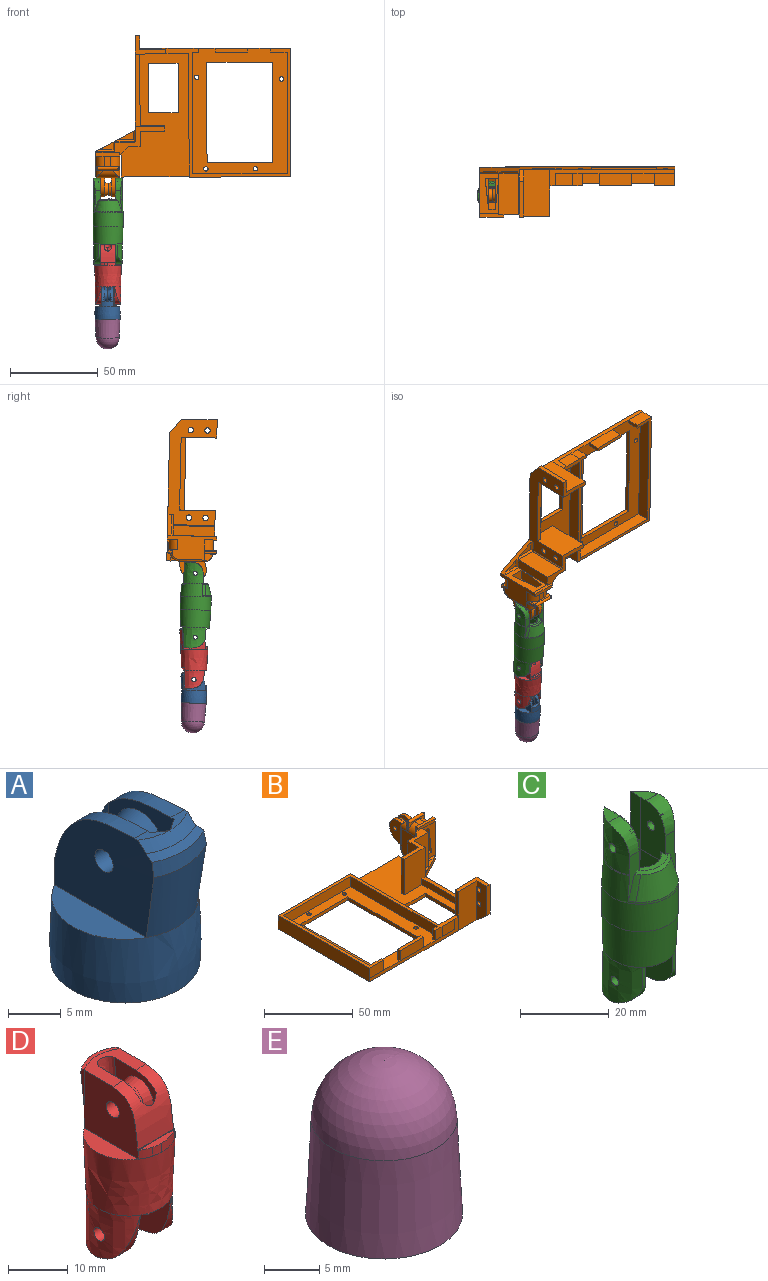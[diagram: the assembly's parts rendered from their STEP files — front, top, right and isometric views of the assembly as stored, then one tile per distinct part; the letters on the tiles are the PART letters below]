
ASSEMBLY  parts=5 mates=4
PART A: 32 faces, bbox 15x16.1x19 mm
  f0: bspline ~6.52x6.52mm, area 30.3mm2, adj f2,f3
  f1: plane 6.53x6.53mm, normal (-1,0,0), area 28.8mm2, adj f2,f31
  f2: bspline ~6.52x6.52mm, area 30.3mm2, adj f0,f1
  f3: plane 13x9.4mm, normal (-1,0,0), area 76.2mm2, adj f0,f4,f8,f11,f17,f19,f26,f27
  f4: plane 6.65x3.21mm, normal (0,0,1), area 9.7mm2, adj f3,f8,f9,f10,f12,f19,f20,f26
  f5: plane 3.24x1.42mm, normal (0,0,1), area 2.2mm2, adj f6,f9,f18,f20,f21
  f6: plane 13.3x11.06mm, normal (-1,0,0), area 116.5mm2, adj f5,f12,f15,f20,f21,f23,f24,f25
  f7: plane 12.34x11.06mm, normal (1,0,0), area 111mm2, adj f11,f12,f16,f19,f21,f22,f31
  f8: plane 5.75x3.05mm, normal (-0.96,0.27,0), area 7.6mm2, adj f3,f4,f19
  f9: plane 13x9.4mm, normal (1,0,0), area 104.9mm2, adj f4,f5,f10,f18,f20,f26,f27,f30
  f10: plane 5.75x3.05mm, normal (0.96,0.27,0), area 7.6mm2, adj f4,f9,f20
  f11: plane 3.24x1.42mm, normal (0,0,1), area 2.2mm2, adj f3,f7,f17,f19,f21
  f12: bspline ~8.52x3.23mm, area 22.2mm2, adj f4,f6,f7,f14
  f13: plane 14.18x14.18mm, normal (0,0,-1), area 149.3mm2, adj f14,f28,f29
  f14: bspline ~14.35x14.35mm, area 327.8mm2, adj f12,f13,f15,f16,f23
  f15: plane 12.33x3.71mm, normal (0,0,1), area 31.9mm2, adj f6,f14
  f16: plane 12.36x3.74mm, normal (0,0,1), area 31.9mm2, adj f7,f14
  f17: plane 12.71x1.56mm, normal (-0.56,0.83,0), area 24mm2, adj f3,f11,f18,f21,f27
  f18: plane 12.71x1.56mm, normal (0.56,0.83,0), area 24mm2, adj f5,f9,f17,f21,f27
  f19: extruded ~10.69x7.52mm, area 23.8mm2, adj f3,f4,f7,f8,f11
  f20: extruded ~10.69x7.52mm, area 23.8mm2, adj f4,f5,f6,f9,f10
  f21: bspline ~8.22x2.15mm, area 9.9mm2, adj f5,f6,f7,f11,f17,f18,f25
  f22: plane 9.73x0.86mm, normal (0.55,0.84,0), area 5.5mm2, adj f7,f23,f24,f25
  f23: bspline ~7.5x7.44mm, area 55.3mm2, adj f6,f14,f22,f24
  f24: bspline ~7.5x1.72mm, area 12.7mm2, adj f6,f22,f23,f25
  f25: bspline ~7.28x1.87mm, area 6.8mm2, adj f6,f21,f22,f24
  f26: cylinder r=2.84mm len=5.19mm, axis (0,0,1), area 17.1mm2, adj f3,f4,f9,f27
  f27: plane 10.93x3.12mm, normal (0,0,1), area 23.5mm2, adj f3,f9,f17,f18,f26,f28,f29
  f28: cylinder r=1.16mm len=5.33mm, axis (0,0,-1), area 39mm2, adj f13,f27
  f29: cylinder r=1.16mm len=5.33mm, axis (0,0,-1), area 38.9mm2, adj f13,f27
  f30: cylinder r=1.22mm len=2.43mm, axis (-1,0,0), area 13.5mm2, adj f6,f9
  f31: cylinder r=1.22mm len=4.8mm, axis (-1,0,0), area 36.7mm2, adj f1,f7
PART B: 149 faces, bbox 111.3x92x28.5 mm
  f0: plane 60.18x26.89mm, normal (1,0,0), area 702.9mm2, adj f9,f23,f24,f32,f60,f63,f68,f70
  f1: plane 13.52x2.01mm, normal (0,-1,0), area 25.2mm2, adj f4,f21,f31,f63,f78,f94
  f2: plane 9.17x4.88mm, normal (0,0,1), area 22.4mm2, adj f32,f147,f148
  f3: plane 0.5x0.13mm, normal (0,-1,0), area 0mm2, adj f104,f117,f141
  f4: plane 27.22x13.53mm, normal (-1,0,0), area 230.8mm2, adj f1,f12,f63,f93,f94,f97,f99,f104
  f5: plane 14.04x11.79mm, normal (0,1,0), area 54mm2, adj f7,f16,f17,f107,f108,f110,f121,f124
  f6: plane 8.39x3.75mm, normal (0,-0.18,0.98), area 31.8mm2, adj f19,f20,f79,f91,f92,f108
  f7: extruded ~10.9x7.85mm, area 33.1mm2, adj f5,f10,f17,f85,f92
  f8: plane 83.12x9.32mm, normal (0,1,0), area 598.9mm2, adj f9,f12,f30,f42,f45,f106
  f9: plane 111x73.01mm, normal (0,0,-1), area 4099.4mm2, adj f0,f8,f26,f27,f28,f29,f30,f31
  f10: plane 2.53x2.22mm, normal (0,1,0), area 5.6mm2, adj f7,f17,f85,f88
  f11: plane 2.53x2.13mm, normal (0,1,0), area 5.4mm2, adj f15,f16,f90,f107
  f12: plane 70.48x39.53mm, normal (0,0,1), area 1630.3mm2, adj f4,f8,f24,f26,f27,f28,f41,f45
  f13: plane 6x3.53mm, normal (0,0,1), area 21.1mm2, adj f93,f96,f97,f98
  f14: plane 8.29x0mm, normal (0,0,1), area 0mm2, adj f15,f91,f107
  f15: plane 13.03x11.25mm, normal (-1,0,0), area 75.3mm2, adj f11,f14,f18,f19,f87,f90,f107,f110
  f16: plane 16.08x11.25mm, normal (1,0,0), area 134.2mm2, adj f5,f11,f89,f90,f107,f110
  f17: plane 16.08x11.25mm, normal (-1,0,0), area 134.2mm2, adj f5,f7,f10,f88,f89,f110
  f18: plane 3.72x0.75mm, normal (0,1,0), area 2.8mm2, adj f15,f84,f85,f110
  f19: plane 17.65x8.49mm, normal (-1,0,0), area 126mm2, adj f6,f15,f79,f84,f91
  f20: plane 17.65x8.49mm, normal (1,0,0), area 126mm2, adj f6,f79,f84,f85,f92
  f21: plane 22.91x10.84mm, normal (0,-1,0), area 145.8mm2, adj f1,f31,f78,f80,f81,f82,f83,f145
  f22: plane 7.94x4.22mm, normal (0,0,1), area 16.8mm2, adj f32,f145,f146
  f23: plane 20.29x2.59mm, normal (0,-1,0), area 52.5mm2, adj f0,f60,f62,f76
  f24: plane 30.4x24.56mm, normal (0,1,0), area 507.8mm2, adj f0,f12,f42,f45,f59,f60,f70,f71
  f25: plane 71x54mm, normal (0,0,1), area 1615.6mm2, adj f29,f33,f34,f35,f36,f37,f38,f39
  f26: plane 17.02x2.33mm, normal (0,-1,0), area 39.6mm2, adj f9,f12,f27,f41
  f27: plane 28.12x2.33mm, normal (1,0,0), area 65.5mm2, adj f9,f12,f26,f28
  f28: plane 17.02x2.33mm, normal (0,1,0), area 39.6mm2, adj f9,f12,f27,f41
  f29: plane 70.93x9.33mm, normal (0,-1,0), area 186.1mm2, adj f9,f25,f30,f42,f43,f44,f46,f55
  f30: plane 73x9.32mm, normal (-1,0,0), area 680.7mm2, adj f8,f9,f29,f42,f46
  f31: plane 28.22x13.51mm, normal (1,0,0), area 250.7mm2, adj f1,f9,f21,f32,f93,f94,f98,f99
  f32: plane 22.64x12.04mm, normal (0.47,-0.88,0), area 62.7mm2, adj f0,f2,f9,f22,f31,f145,f146,f147
  f33: plane 56.99x2.33mm, normal (1,0,0), area 132.7mm2, adj f9,f25,f34,f40
  f34: plane 37.47x2.33mm, normal (0,1,0), area 87.2mm2, adj f9,f25,f33,f35
  f35: plane 56.99x2.33mm, normal (-1,0,0), area 132.7mm2, adj f9,f25,f34,f40
  f36: cylinder r=1.25mm len=2.5mm, axis (0,0,-1), area 18.3mm2, adj f9,f25
  f37: cylinder r=1.25mm len=2.5mm, axis (0,0,-1), area 18.3mm2, adj f9,f25
  f38: cylinder r=1.25mm len=2.5mm, axis (0,0,-1), area 18.3mm2, adj f9,f25
  f39: cylinder r=1.25mm len=2.5mm, axis (0,0,-1), area 18.3mm2, adj f9,f25
  f40: plane 37.47x2.33mm, normal (0,-1,0), area 87.2mm2, adj f9,f25,f33,f35
  f41: plane 28.12x2.33mm, normal (-1,0,0), area 65.5mm2, adj f9,f12,f26,f28
  f42: plane 73.01x70.92mm, normal (0,0,1), area 455mm2, adj f8,f24,f29,f30,f43,f44,f45,f46
  f43: plane 7x5.46mm, normal (0,-1,0), area 38.1mm2, adj f29,f42,f44,f53
  f44: plane 9.98x7mm, normal (0,-1,0), area 69.8mm2, adj f29,f42,f43
  f45: plane 70.48x7mm, normal (1,0,0), area 493.1mm2, adj f8,f12,f24,f42
  f46: plane 11.5x7mm, normal (0,-1,0), area 80.5mm2, adj f29,f30,f42,f47
  f47: plane 7x2mm, normal (1,0,0), area 14mm2, adj f25,f42,f46,f48
  f48: plane 9.5x7mm, normal (0,1,0), area 66.4mm2, adj f25,f42,f47,f49
  f49: plane 68.99x7mm, normal (1,0,0), area 482.7mm2, adj f25,f42,f48,f50
  f50: plane 54x7mm, normal (0,-1,0), area 377.8mm2, adj f25,f42,f49,f51
  f51: plane 68.99x7mm, normal (-1,0,0), area 482.7mm2, adj f25,f42,f50,f52
  f52: plane 7x3.5mm, normal (0,1,0), area 24.5mm2, adj f25,f42,f51,f53
  f53: plane 7x2.01mm, normal (-1,0,0), area 14mm2, adj f25,f42,f43,f52
  f54: plane 18.5x2mm, normal (0,0,1), area 37.1mm2, adj f55,f56,f57,f58
  f55: plane 18.5x7mm, normal (0,-1,0), area 129.4mm2, adj f29,f54,f56,f57
  f56: plane 7x2.01mm, normal (1,0,0), area 14mm2, adj f25,f54,f55,f58
  f57: plane 7x2.01mm, normal (-1,0,0), area 14mm2, adj f25,f54,f55,f58
  f58: plane 18.5x7mm, normal (0,1,0), area 129.4mm2, adj f25,f54,f56,f57
  f59: plane 17.57x2.52mm, normal (-1,0,0), area 44.3mm2, adj f24,f42,f60,f61
  f60: plane 17.43x10.36mm, normal (0,0,1), area 64.2mm2, adj f0,f23,f24,f59,f61,f62
  f61: plane 26.89x14.85mm, normal (0,-1,0), area 399.2mm2, adj f9,f29,f59,f60,f62,f69
  f62: plane 26.89x7.84mm, normal (-1,0,0), area 169.9mm2, adj f23,f60,f61,f74,f75,f76
  f63: plane 28.55x16.27mm, normal (0,0,1), area 113.7mm2, adj f0,f1,f4,f64,f65,f66,f67,f68
  f64: plane 24.56x6.7mm, normal (0,1,0), area 164.6mm2, adj f12,f63,f65,f143
  f65: plane 24.56x8.75mm, normal (-1,0,0), area 200mm2, adj f12,f63,f64,f66,f72,f73
  f66: plane 24.56x14.14mm, normal (0,1,0), area 347.2mm2, adj f12,f63,f65,f67
  f67: plane 24.56x2.5mm, normal (-1,0,0), area 61.5mm2, adj f12,f63,f66,f68
  f68: plane 24.56x16.72mm, normal (0,-1,0), area 399.7mm2, adj f0,f12,f63,f67,f70,f71
  f69: plane 2.33x0mm, normal (-1,0,0), area 0mm2, adj f9,f29,f61
  f70: plane 41.42x2.59mm, normal (0,0,1), area 107.1mm2, adj f0,f24,f68,f71
  f71: plane 41.42x4.28mm, normal (-1,0,0), area 177.2mm2, adj f12,f24,f68,f70
  f72: cylinder r=1.54mm len=3.08mm, axis (1,0,0), area 25mm2, adj f0,f65
  f73: cylinder r=1.54mm len=3.08mm, axis (1,0,0), area 25mm2, adj f0,f65
  f74: cylinder r=1.54mm len=3.08mm, axis (1,0,0), area 25.1mm2, adj f0,f62
  f75: cylinder r=1.54mm len=3.08mm, axis (1,0,0), area 25mm2, adj f0,f62
  f76: plane 7.84x6.61mm, normal (0,-0.64,-0.76), area 26.5mm2, adj f0,f9,f23,f62
  f77: plane 23.56x11.33mm, normal (0,-1,0), area 266.9mm2, adj f63,f78,f144,f147
  f78: plane 23.56x5.64mm, normal (1,0,0), area 132.8mm2, adj f1,f21,f63,f77,f146
  f79: plane 17.66x7.79mm, normal (0,-1,0), area 36.2mm2, adj f6,f19,f20,f80,f81,f82,f83,f84
  f80: plane 7.79x6.03mm, normal (0,0,1), area 47mm2, adj f21,f79,f81,f83
  f81: plane 17.65x6.03mm, normal (-0.99,0,-0.11), area 107.1mm2, adj f21,f79,f80,f82
  f82: plane 6.03x3.77mm, normal (0,0,-1), area 22.7mm2, adj f21,f79,f81,f83
  f83: plane 17.66x6.03mm, normal (0.99,0,-0.11), area 107.2mm2, adj f21,f79,f80,f82
  f84: plane 8.48x3.75mm, normal (0,-0.38,-0.92), area 34.2mm2, adj f18,f19,f20,f79
  f85: plane 12.65x11.26mm, normal (1,0,0), area 65.4mm2, adj f7,f10,f18,f20,f86,f88,f92,f110
  f86: bspline ~7.74x7.74mm, area 43.1mm2, adj f85,f87
  f87: bspline ~7.8x7.8mm, area 45.1mm2, adj f15,f86
  f88: extruded ~10.9x4.86mm, area 29.8mm2, adj f10,f17,f85,f110
  f89: cylinder r=1.27mm len=8.08mm, axis (1,0,0), area 64.5mm2, adj f16,f17
  f90: extruded ~10.9x4.86mm, area 28.6mm2, adj f11,f15,f16,f110
  f91: plane 9.28x2.67mm, normal (-1,0,0), area 18.4mm2, adj f6,f14,f19,f107,f108
  f92: plane 11.19x5.03mm, normal (1,0,0), area 28.8mm2, adj f6,f7,f20,f85,f108
  f93: plane 13.52x7mm, normal (0,1,0), area 37.8mm2, adj f4,f13,f31,f94,f97,f98
  f94: plane 13.52x2mm, normal (0,0,1), area 27mm2, adj f1,f4,f31,f93
  f95: plane 12.53x3.82mm, normal (0,1,0), area 19.7mm2, adj f109,f110,f111,f113,f133,f135
  f96: plane 12.53x3.82mm, normal (0,-1,0), area 19.7mm2, adj f13,f97,f98,f113,f137,f139
  f97: cylinder r=5mm len=6.5mm, axis (0,1,0), area 47.7mm2, adj f4,f13,f93,f96,f139
  f98: cylinder r=5mm len=6.52mm, axis (0,1,0), area 47.7mm2, adj f13,f31,f93,f96,f137
  f99: plane 14.52x6mm, normal (0,1,0), area 21.4mm2, adj f4,f9,f12,f31,f101,f102,f103,f104
  f100: plane 5.08x5.08mm, normal (0,-1,0), area 4.5mm2, adj f31,f102,f117,f125,f131
  f101: plane 7.53x6mm, normal (0,0,-1), area 45.1mm2, adj f99,f102,f104,f117
  f102: cylinder r=5mm len=6.02mm, axis (0,-1,0), area 47.1mm2, adj f31,f99,f100,f101
  f103: plane 12.51x2.33mm, normal (1,0,0), area 29.1mm2, adj f9,f12,f99,f105
  f104: cylinder r=1mm len=6.5mm, axis (0,1,0), area 9.7mm2, adj f3,f4,f99,f101,f141
  f105: plane 13.36x2.33mm, normal (0,1,0), area 31.1mm2, adj f9,f12,f103,f106
  f106: plane 2.33x0mm, normal (1,0,0), area 0mm2, adj f8,f9,f12,f105
  f107: extruded ~10.9x7.85mm, area 31.8mm2, adj f5,f11,f14,f15,f16,f91
  f108: plane 3.72x0.51mm, normal (0,0.98,0.18), area 1.9mm2, adj f5,f6,f91,f92
  f109: cylinder r=5mm len=5mm, axis (0,1,0), area 20.2mm2, adj f4,f95,f110,f124,f135
  f110: cylinder r=5mm len=12.95mm, axis (1,0,0), area 72.8mm2, adj f5,f15,f16,f17,f18,f85,f88,f90
  f111: cylinder r=5mm len=5.01mm, axis (0,1,0), area 20.2mm2, adj f31,f95,f110,f126,f133
  f112: cylinder r=1mm len=1mm, axis (0,-1,0), area 0.8mm2, adj f4,f136,f140
  f113: cylinder r=1mm len=12.53mm, axis (1,0,0), area 37.8mm2, adj f95,f96,f134,f136,f138,f140
  f114: cylinder r=1mm len=1mm, axis (0,-1,0), area 0.8mm2, adj f31,f134,f138
  f115: plane 2.1x1.01mm, normal (1,0,0), area 2mm2, adj f118,f125,f127,f131
  f116: plane 12.55x1.18mm, normal (0,1,0), area 12.9mm2, adj f117,f122,f123,f125,f127,f129
  f117: cylinder r=1mm len=12.53mm, axis (-1,0,0), area 37.8mm2, adj f3,f100,f101,f116,f128,f130,f132,f142
  f118: cylinder r=1mm len=1mm, axis (0,-1,0), area 0.8mm2, adj f115,f128,f132
  f119: cylinder r=1mm len=1mm, axis (0,-1,0), area 0.8mm2, adj f4,f130,f142
  f120: plane 11.53x0.2mm, normal (0,1,0), area 2.4mm2, adj f121,f122,f124,f126
  f121: plane 11.79x0.02mm, normal (0,0,1), area 0.1mm2, adj f5,f120,f124,f126
  f122: cylinder r=5mm len=11.54mm, axis (-1,0,0), area 85mm2, adj f116,f120,f123,f125
  f123: bspline ~5.87x5mm, area 10.9mm2, adj f4,f116,f122,f124,f129
  f124: cylinder r=1mm len=15.89mm, axis (0,0,1), area 20.6mm2, adj f4,f5,f109,f110,f120,f121,f123
  f125: torus R=4mm, axis (-1,0,0), area 11.2mm2, adj f31,f100,f115,f116,f122,f126,f127,f131
  f126: cylinder r=1mm len=15.92mm, axis (0,0,-1), area 22.9mm2, adj f5,f31,f110,f111,f120,f121,f125
  f127: cylinder r=0.5mm len=1.93mm, axis (0,0,-1), area 1.2mm2, adj f115,f116,f125,f128
  f128: bspline ~1.19x1mm, area 0.5mm2, adj f117,f118,f127
  f129: cylinder r=0.5mm len=2mm, axis (0,0,1), area 1.2mm2, adj f4,f116,f123,f130
  f130: bspline ~1.19x1mm, area 0.5mm2, adj f117,f119,f129
  f131: cylinder r=0.5mm len=2.09mm, axis (0,0,-1), area 1.4mm2, adj f100,f115,f125,f132
  f132: bspline ~1.05x1mm, area 0.5mm2, adj f117,f118,f131
  f133: cylinder r=0.5mm len=6mm, axis (0,0,1), area 3.9mm2, adj f31,f95,f111,f134
  f134: bspline ~1.19x1mm, area 0.5mm2, adj f113,f114,f133
  f135: cylinder r=0.5mm len=6mm, axis (0,0,-1), area 3.9mm2, adj f4,f95,f109,f136
  f136: bspline ~1.19x1mm, area 0.5mm2, adj f112,f113,f135
  f137: cylinder r=0.5mm len=6mm, axis (0,0,-1), area 3.9mm2, adj f31,f96,f98,f138
  f138: bspline ~1.19x1mm, area 0.5mm2, adj f113,f114,f137
  f139: cylinder r=0.5mm len=6mm, axis (0,0,1), area 3.9mm2, adj f4,f96,f97,f140
  f140: bspline ~1.05x1mm, area 0.5mm2, adj f112,f113,f139
  f141: cylinder r=0.5mm len=1mm, axis (0,0,1), area 0.4mm2, adj f3,f4,f104,f142
  f142: bspline ~1.19x1mm, area 0.5mm2, adj f117,f119,f141
  f143: plane 24.56x5.02mm, normal (-0.71,0.71,0), area 174.3mm2, adj f4,f12,f63,f64
  f144: plane 23.81x0.5mm, normal (0.71,-0.71,0), area 16.8mm2, adj f0,f63,f77,f147,f148
  f145: plane 10.82x1mm, normal (0,-0.71,0.71), area 13.3mm2, adj f21,f22,f32,f146
  f146: plane 5.71x1.01mm, normal (0.71,0,0.71), area 7mm2, adj f22,f32,f78,f145,f147
  f147: plane 11.65x1mm, normal (0,-0.71,0.71), area 14.9mm2, adj f2,f32,f77,f144,f146,f148
  f148: plane 6.16x1mm, normal (0.71,0,0.71), area 7.9mm2, adj f0,f2,f32,f144,f147
PART C: 81 faces, bbox 22.7x23.4x54.2 mm
  f0: extruded ~10.97x4.02mm, area 4.2mm2, adj f12,f27,f32,f47
  f1: extruded ~6.78x6.05mm, area 36.1mm2, adj f28,f42,f44,f67,f78,f79
  f2: plane 0.55x0.32mm, normal (0,-0.03,-1), area 0.1mm2, adj f4,f15,f72
  f3: extruded ~1x0.52mm, area 0.7mm2, adj f4,f5,f70
  f4: plane 14.35x7.78mm, normal (1,0,0), area 93.4mm2, adj f2,f3,f5,f9,f27,f31,f66,f69
  f5: extruded ~6.78x6.05mm, area 34.9mm2, adj f3,f4,f10,f27,f47,f70
  f6: extruded ~8.33x2.52mm, area 23.3mm2, adj f7,f17,f73,f76
  f7: plane 8.37x3.28mm, normal (0,0,1), area 13.3mm2, adj f6,f8,f12,f80
  f8: plane 12.51x3.2mm, normal (-1,0,0), area 36.2mm2, adj f7,f30,f40,f41,f44,f73,f80
  f9: plane 4.86x3.73mm, normal (0,0,1), area 11.5mm2, adj f4,f10,f12,f45,f47,f69,f75
  f10: plane 3.48x0.01mm, normal (0,-0.71,0.71), area 0mm2, adj f5,f9,f47,f69
  f11: cylinder r=1.16mm len=3.76mm, axis (1,0,0), area 27.4mm2, adj f47,f71
  f12: plane 12.51x3.19mm, normal (1,0,0), area 36.1mm2, adj f0,f7,f9,f46,f47,f76,f80
  f13: bspline ~3.53x1.19mm, area 1.2mm2, adj f14,f15,f54,f65
  f14: offset ~11.35x7.15mm, area 0.7mm2, adj f13,f16,f54,f64
  f15: offset ~11.36x7.87mm, area 1.3mm2, adj f2,f13,f54,f66
  f16: offset ~17.51x11.38mm, area 41.8mm2, adj f14,f18,f21,f22,f54,f63
  f17: offset ~17.78x10.26mm, area 49.7mm2, adj f6,f20,f23,f54,f72,f77
  f18: offset ~20.18x12.8mm, area 1.9mm2, adj f16,f20,f22,f24,f54
  f19: offset ~11.38x7.84mm, area 1.1mm2, adj f20,f21,f61,f77
  f20: plane 35.36x13.78mm, normal (-1,0,0), area 320.5mm2, adj f17,f18,f19,f21,f22,f23,f24,f25
  f21: bspline ~4.41x2.16mm, area 5.4mm2, adj f16,f19,f20,f22,f62
  f22: offset ~5.9x5.8mm, area 0.2mm2, adj f16,f18,f20,f21
  f23: extruded ~8.65x7.49mm, area 72.2mm2, adj f17,f20,f38,f54
  f24: extruded ~8.65x7.47mm, area 72.1mm2, adj f18,f20,f25,f54
  f25: offset ~31.33x22.73mm, area 99.2mm2, adj f20,f24,f36,f54
  f26: plane 9.14x4.96mm, normal (0,0.03,-1), area 23.4mm2, adj f20,f37,f38,f54
  f27: plane 12.53x3.95mm, normal (0,-1,0), area 21.7mm2, adj f0,f4,f5,f31,f32,f33,f35,f47
  f28: plane 12.63x4.05mm, normal (0,-1,0), area 21.8mm2, adj f1,f30,f31,f32,f33,f34,f44,f78
  f29: extruded ~17.39x17.12mm, area 411.9mm2, adj f32,f37
  f30: extruded ~10.97x4.03mm, area 4.4mm2, adj f8,f28,f32,f44
  f31: plane 9.7x3.99mm, normal (0,0,1), area 14mm2, adj f4,f27,f28,f33,f61,f62,f63,f64
  f32: bspline ~17.37x17.11mm, area 256.2mm2, adj f0,f27,f28,f29,f30,f34,f35,f80
  f33: bspline ~11.36x3.43mm, area 11.5mm2, adj f27,f28,f31,f34,f35
  f34: bspline ~14.35x6.39mm, area 95mm2, adj f28,f32,f33,f35
  f35: bspline ~6.36x3.02mm, area 10.5mm2, adj f27,f32,f33,f34
  f36: plane 10.5x4.5mm, normal (0,0.03,-1), area 24mm2, adj f20,f25,f37,f52,f54,f59
  f37: bspline ~17.37x17.11mm, area 527.1mm2, adj f26,f29,f36,f48,f55
  f38: offset ~17.94x14.96mm, area 95.5mm2, adj f20,f23,f26,f54
  f39: plane 0.08x0mm, normal (-0.03,-0.38,0.92), area 0mm2, adj f40,f41,f44
  f40: plane 0.07x0.04mm, normal (-0.03,0,1), area 0mm2, adj f8,f39,f44
  f41: plane 4.86x3.73mm, normal (0,0,1), area 11.6mm2, adj f8,f39,f42,f44,f74,f78
  f42: plane 3.72x0.02mm, normal (0,-0.71,0.71), area 0mm2, adj f1,f41,f44,f67,f78
  f43: cylinder r=1.16mm len=3.93mm, axis (1,0,0), area 28.7mm2, adj f44,f68
  f44: extruded ~11.84x10.99mm, area 135.4mm2, adj f1,f8,f28,f30,f39,f40,f41,f42
  f45: plane 0.08x0mm, normal (0.02,-0.38,0.92), area 0mm2, adj f9,f46,f47
  f46: plane 0.07x0.04mm, normal (0.02,0,1), area 0mm2, adj f12,f45,f47
  f47: extruded ~11.85x10.99mm, area 135.4mm2, adj f0,f5,f9,f10,f11,f12,f27,f45
  f48: extruded ~13.64x12.22mm, area 153.8mm2, adj f37,f49,f50,f51,f52,f53
  f49: plane 3.58x3.53mm, normal (0,0.03,-1), area 9.6mm2, adj f20,f48,f50,f51
  f50: plane 12.03x1.68mm, normal (0,1,-0.07), area 9.7mm2, adj f20,f48,f49
  f51: extruded ~8.78x6.02mm, area 32.9mm2, adj f20,f48,f49,f52
  f52: plane 5.61x0.92mm, normal (0,-1,-0.03), area 5.1mm2, adj f20,f36,f48,f51
  f53: cylinder r=1.15mm len=3.89mm, axis (1,0,0), area 27.6mm2, adj f20,f48
  f54: plane 35x13.42mm, normal (1,0,0), area 315.4mm2, adj f13,f14,f15,f16,f17,f18,f23,f24
  f55: extruded ~13.64x12.23mm, area 153.8mm2, adj f37,f56,f57,f58,f59,f60
  f56: plane 3.58x3.53mm, normal (0,0.03,-1), area 9.6mm2, adj f54,f55,f57,f58
  f57: plane 12.03x1.65mm, normal (0,1,-0.07), area 9.7mm2, adj f54,f55,f56
  f58: extruded ~8.78x6.02mm, area 32.9mm2, adj f54,f55,f56,f59
  f59: plane 5.61x0.92mm, normal (0,-1,-0.03), area 5.1mm2, adj f36,f54,f55,f58
  f60: cylinder r=1.15mm len=3.9mm, axis (1,0,0), area 27.7mm2, adj f54,f55
  f61: extruded ~2.5x0.7mm, area 2.1mm2, adj f19,f31,f62,f78
  f62: extruded ~2.51x1.07mm, area 3.6mm2, adj f21,f31,f61,f63
  f63: extruded ~6.04x2.52mm, area 16.6mm2, adj f16,f31,f62,f64
  f64: extruded ~2.5x0.15mm, area 0.5mm2, adj f14,f31,f63,f65
  f65: extruded ~2.5x0.38mm, area 1.2mm2, adj f13,f31,f64,f66
  f66: extruded ~2.5x0.54mm, area 1.6mm2, adj f4,f15,f31,f65
  f67: extruded ~4.34x1.82mm, area 0.3mm2, adj f1,f42,f78,f79
  f68: extruded ~2.33x2.33mm, area 0.5mm2, adj f43,f78
  f69: plane 0.24x0mm, normal (0,-0.71,0.71), area 0mm2, adj f4,f9,f10,f70
  f70: extruded ~4.05x1.53mm, area 1.1mm2, adj f3,f4,f5,f69
  f71: extruded ~2.33x2.33mm, area 1.8mm2, adj f4,f11
  f72: plane 5.92x0.24mm, normal (0,0,-1), area 1.4mm2, adj f2,f4,f17,f54,f76
  f73: plane 14.32x0.11mm, normal (-1,0,0), area 1.1mm2, adj f6,f8,f74,f77,f78
  f74: plane 0.07x0.07mm, normal (0,0,1), area 0mm2, adj f41,f73
  f75: plane 0.27x0.24mm, normal (0,0,1), area 0mm2, adj f9,f76
  f76: plane 14.32x0.3mm, normal (1,0,0), area 3.9mm2, adj f4,f6,f12,f72,f75
  f77: plane 6.78x0.51mm, normal (0,0,-1), area 0.4mm2, adj f17,f19,f20,f73,f78
  f78: plane 14.36x7.98mm, normal (-1,0,0), area 95.9mm2, adj f1,f28,f31,f41,f42,f61,f67,f68
  f79: extruded ~1x0.17mm, area 0.2mm2, adj f1,f67,f78
  f80: bspline ~9.33x2.21mm, area 10.2mm2, adj f7,f8,f12,f32
PART D: 58 faces, bbox 15.6x16.5x34.3 mm
  f0: plane 12.5x1.44mm, normal (0.15,-0.99,0), area 18mm2, adj f1,f2,f4,f6,f14,f42,f52,f53
  f1: plane 3.62x1.27mm, normal (0,0,1), area 0.9mm2, adj f0,f2,f4,f43,f44,f52,f53
  f2: plane 11.83x1.5mm, normal (0.61,-0.8,0), area 22.3mm2, adj f0,f1,f14,f43,f52
  f3: plane 3.64x1.04mm, normal (0,0,1), area 2.7mm2, adj f5,f32,f33,f41
  f4: cylinder r=1.92mm len=11.91mm, axis (0,0,-1), area 5mm2, adj f0,f1,f5,f6,f32,f44,f45,f54
  f5: plane 11.96x8.84mm, normal (1,0,0), area 57.2mm2, adj f3,f4,f6,f26,f33,f41,f47,f49
  f6: plane 8.38x1.12mm, normal (0,0,-1), area 9.1mm2, adj f0,f4,f5,f41,f42
  f7: plane 12.78x12.01mm, normal (1,0,0), area 132.6mm2, adj f8,f9,f26,f30,f35,f47,f51,f57
  f8: plane 15.36x7.71mm, normal (0,0,1), area 31.4mm2, adj f7,f9,f15,f30
  f9: cylinder r=7.58mm len=5.73mm, axis (0,0,-1), area 12.5mm2, adj f7,f8,f10,f31,f35,f36
  f10: plane 0.43x0.01mm, normal (0,0,1), area 0mm2, adj f9,f15
  f11: plane 13.81x5.6mm, normal (0,0,1), area 30.9mm2, adj f15,f27,f28
  f12: plane 3.99x3.54mm, normal (0,0,-1), area 10.9mm2, adj f16,f17,f18,f23
  f13: plane 4.06x3.55mm, normal (0,0,-1), area 10.9mm2, adj f19,f20,f21,f22
  f14: plane 13.06x7.22mm, normal (0,0,-1), area 37.9mm2, adj f0,f2,f15,f16,f20,f40,f41,f42
  f15: bspline ~15.35x15.35mm, area 537.2mm2, adj f8,f10,f11,f14,f17,f18,f19,f21
  f16: plane 11.16x10.41mm, normal (-1,0,0), area 92.9mm2, adj f12,f14,f17,f23,f25,f46
  f17: plane 11.69x1.7mm, normal (-0.14,0.99,0), area 16.7mm2, adj f12,f15,f16,f18,f46
  f18: extruded ~11.37x10.16mm, area 107.2mm2, adj f12,f15,f17,f23,f25
  f19: plane 11.68x1.63mm, normal (0.19,0.98,0), area 16.1mm2, adj f13,f15,f20,f21,f46
  f20: plane 11.16x10.41mm, normal (1,0,0), area 92.9mm2, adj f13,f14,f19,f21,f22,f24,f46
  f21: extruded ~11.43x10.16mm, area 108mm2, adj f13,f15,f19,f20,f22,f24
  f22: extruded ~10.14x7.39mm, area 22.6mm2, adj f13,f20,f21
  f23: extruded ~10.16x7.39mm, area 22.6mm2, adj f12,f16,f18
  f24: cylinder r=1.25mm len=3.62mm, axis (-1,0,0), area 28.4mm2, adj f20,f21
  f25: cylinder r=1.25mm len=3.62mm, axis (-1,0,0), area 28.4mm2, adj f16,f18
  f26: plane 8.76x8.54mm, normal (-0.01,-0.01,1), area 39mm2, adj f5,f7,f27,f32,f37,f39,f47,f54
  f27: plane 12.78x11.96mm, normal (-1,0,0), area 132.2mm2, adj f11,f26,f28,f34,f47,f51,f57
  f28: cylinder r=7.57mm len=2.33mm, axis (0,0,-1), area 4.7mm2, adj f11,f15,f27,f29,f48
  f29: extruded ~1.9x1.85mm, area 3.5mm2, adj f15,f28,f30,f48
  f30: cylinder r=7.57mm len=4.23mm, axis (0,0,-1), area 8.4mm2, adj f7,f8,f29,f48
  f31: extruded ~2.09x1.43mm, area 1.5mm2, adj f9,f15,f34,f36
  f32: plane 11.97x10.03mm, normal (-1,0,0), area 63.5mm2, adj f3,f4,f26,f33,f41,f45,f47,f50
  f33: cylinder r=2.84mm len=9.67mm, axis (0,0,-1), area 38.1mm2, adj f3,f5,f32,f47
  f34: cylinder r=7.58mm len=11.9mm, axis (0,0,-1), area 6.9mm2, adj f15,f27,f31,f36,f38
  f35: extruded ~11.96x3.78mm, area 6mm2, adj f7,f9,f36,f37
  f36: cone r=7.36mm half-angle=5deg, axis (-0.01,-0.01,1), area 89.9mm2, adj f9,f31,f34,f35,f37,f38,f56
  f37: plane 9.11x0.96mm, normal (1,0,0.01), area 4.5mm2, adj f26,f35,f36,f39,f56
  f38: plane 8.11x0.85mm, normal (-1,0,-0.01), area 3.6mm2, adj f34,f36,f39,f56
  f39: plane 8.47x2.04mm, normal (-0.01,-0.01,1), area 6.1mm2, adj f26,f37,f38,f56
  f40: plane 12.5x8.03mm, normal (-1,0,0), area 100.3mm2, adj f14,f41,f44,f45
  f41: cylinder r=15mm len=12.5mm, axis (0,0,-1), area 71.5mm2, adj f3,f5,f6,f14,f32,f40,f42,f45
  f42: plane 12.5x8.03mm, normal (1,0,0), area 100.3mm2, adj f0,f6,f14,f41
  f43: plane 11.83x1.5mm, normal (-0.61,-0.8,0), area 22.3mm2, adj f1,f2,f14,f44
  f44: plane 12.5x1.44mm, normal (-0.15,-0.99,0), area 18mm2, adj f1,f4,f14,f40,f43,f45
  f45: plane 8.38x1.15mm, normal (0,0,-1), area 9.3mm2, adj f4,f32,f40,f41,f44
  f46: bspline ~11x3.5mm, area 18.5mm2, adj f14,f15,f16,f17,f19,f20
  f47: extruded ~10.16x8.47mm, area 89.6mm2, adj f5,f7,f26,f27,f32,f33,f57
  f48: plane 8.47x1.3mm, normal (-0.01,-0.01,1), area 7.4mm2, adj f28,f29,f30,f57
  f49: cone r=3.48mm half-angle=14.8deg, axis (-1,0,0), area 38.3mm2, adj f5,f50
  f50: cone r=3.48mm half-angle=14.8deg, axis (1,0,0), area 38.3mm2, adj f32,f49
  f51: cylinder r=1.5mm len=8.47mm, axis (1,0,0), area 79.8mm2, adj f7,f27
  f52: plane 1.73x1.18mm, normal (-0.01,-0.01,1), area 0.6mm2, adj f0,f1,f2,f53
  f53: bspline ~12.01x3.62mm, area 0mm2, adj f0,f1,f52
  f54: bspline ~12.01x3.62mm, area 49.6mm2, adj f4,f26,f32,f55
  f55: plane 9.8x1.17mm, normal (1,-0.02,0), area 5.7mm2, adj f4,f26,f54
  f56: cone r=7.16mm half-angle=9.3deg, axis (0.01,0.01,-1), area 7.3mm2, adj f36,f37,f38,f39
  f57: plane 8.47x0.15mm, normal (-0.01,0,1), area 1.2mm2, adj f7,f27,f47,f48
PART E: 5 faces, bbox 14.2x14.2x17 mm
  f0: sphere r=6.58mm, area 268.1mm2, adj f2
  f1: plane 14.17x14.17mm, normal (0,0,-1), area 73.3mm2, adj f2,f4
  f2: cone r=6.58mm half-angle=2.7deg, axis (0,0,-1), area 451mm2, adj f0,f1
  f3: sphere r=4.68mm, area 136.6mm2, adj f4
  f4: cone r=4.69mm half-angle=2.7deg, axis (0,0,-1), area 323.7mm2, adj f1,f3
PLACE A rot(axis=(0,-0.02,1),180deg) t=(-52.41,-39.24,-24.54)mm
PLACE B rot(axis=(0,0.71,-0.7),179.9deg) t=(8.17,2.57,78.95)mm fixed
PLACE C rot(axis=(1,0,0),1.2deg) t=(-25.28,1.58,-5.31)mm
PLACE D rot(axis=(0.99,-0.11,0),1.1deg) t=(-56.94,10.84,-34.34)mm
PLACE E rot(axis=(-1,0,0),177.6deg) t=(-51.85,-37.94,-51.53)mm
MATE revolute C.f11 <-> B.f89  axis (1,0,0) through (-44.3,-12.85,36.91)mm
MATE fastened A.f13 <-> E.f2  axis (0,0.04,-1) through (-40.17,-11.98,-36.9)mm
MATE revolute D.f24 <-> A.f30  axis (1,0,0) through (-43.52,-12.05,-23.52)mm
MATE revolute D.f49 <-> C.f54  axis (-1,0,0) through (-44.22,-12.86,0.64)mm
